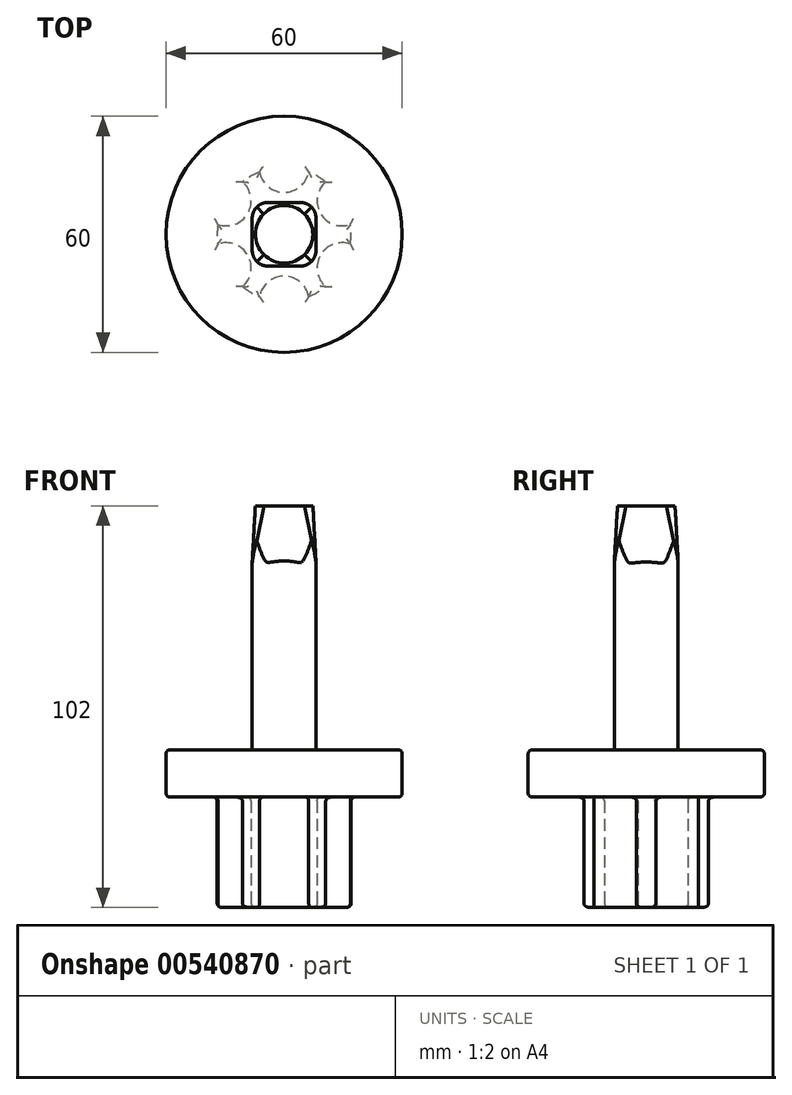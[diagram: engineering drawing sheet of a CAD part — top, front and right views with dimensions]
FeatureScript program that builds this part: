
annotation { "Feature Type Name" : "Feature", "Feature Type Description" : "" }
export const myFeature = defineFeature(function(context is Context, id is Id, definition is map)
    precondition{}
    {
        {
            var Q0;
            Q0=qCreatedBy(makeId("Top.planeOp"),FACE);
            var sketch = newSketch(context, id + "F0", { "sketchPlane" : qUnion([Q0])});
            skCircle(sketch, "E0", {"center": v(0, 0) * mm, "radius": 17 * mm});
            skCircle(sketch, "E1", {"center": v(0, 0) * mm, "radius": 30 * mm});
            skLineSegment(sketch, "E2.bottom", {"start": v(8.1, -8.1) * mm, "end": v(-8.1, -8.1) * mm});
            skLineSegment(sketch, "E2.top", {"start": v(8.1, 8.1) * mm, "end": v(-8.1, 8.1) * mm});
            skLineSegment(sketch, "E2.left", {"start": v(8.1, -8.1) * mm, "end": v(8.1, 8.1) * mm});
            skLineSegment(sketch, "E2.right", {"start": v(-8.1, -8.1) * mm, "end": v(-8.1, 8.1) * mm});
            skCircle(sketch, "E3", {"center": v(0, 0) * mm, "radius": 7 * mm});
            skSolve(sketch);
        }
        {
            var Q0;
            Q0=qCreatedBy(makeId("Top.planeOp"),FACE);
            cPlane(context, id + "F1", {"entities" : qUnion([Q0]), "cplaneType" : CPlaneType.OFFSET, "offset" : 47 * mm, "width" : 150 * mm, "height" : 150 * mm});
        }
        {
            var Q0;
            Q0=qCreatedBy(id+"F1.planeOp",FACE);
            cPlane(context, id + "F2", {"entities" : qUnion([Q0]), "cplaneType" : CPlaneType.OFFSET, "offset" : 15 * mm, "width" : 150 * mm, "height" : 150 * mm});
        }
        {
            var Q0;
            Q0=makeQuery(id+"F0.imprint","IMPRINT",FACE,{"disambiguationData":[TD([[makeQuery(id+"F0.imprint","IMPRINT",EDGE,{"derivedFrom":sQuery(id+"F0.wireOp",EDGE,"E2.bottom")}),-1.0]])]});
            var Q1;
            Q1=makeQuery(id+"F0.imprint","IMPRINT",FACE,{"disambiguationData":[TD([[makeQuery(id+"F0.imprint","IMPRINT",EDGE,{"derivedFrom":sQuery(id+"F0.wireOp",EDGE,"E3")}),1.0]])]});
            var Q2;
            Q2=qCreatedBy(id+"F2.planeOp",FACE);
            extrude(context, id + "F3", {"entities" : qUnion([Q0, Q1]), "endBound" : BoundingType.UP_TO_SURFACE, "depth" : 60 * mm, "endBoundEntityFace" : qUnion([Q2]), "offsetDistance" : 25 * mm});
        }
        {
            var Q0;
            Q0=makeQuery(id+"F3.opExtrude","SWEPT_EDGE",EDGE,{"disambiguationData":[OSD([sQuery(id+"F0.wireOp",EDGE,"E2.bottom"),sQuery(id+"F0.wireOp",EDGE,"E2.left")])]});
            var Q1;
            Q1=makeQuery(id+"F3.opExtrude","SWEPT_EDGE",EDGE,{"disambiguationData":[OSD([sQuery(id+"F0.wireOp",EDGE,"E2.top"),sQuery(id+"F0.wireOp",EDGE,"E2.left")])]});
            var Q2;
            Q2=makeQuery(id+"F3.opExtrude","SWEPT_EDGE",EDGE,{"disambiguationData":[OSD([sQuery(id+"F0.wireOp",EDGE,"E2.bottom"),sQuery(id+"F0.wireOp",EDGE,"E2.right")])]});
            var Q3;
            Q3=makeQuery(id+"F3.opExtrude","SWEPT_EDGE",EDGE,{"disambiguationData":[OSD([sQuery(id+"F0.wireOp",EDGE,"E2.top"),sQuery(id+"F0.wireOp",EDGE,"E2.right")])]});
            fillet(context, id + "F4", {"entities" : qUnion([Q0, Q1, Q2, Q3]), "radius" : 4 * mm, "tangentPropagation" : true, "allowEdgeOverflow" : false});
        }
        {
            var Q0;
            Q0=makeQuery(id+"F0.imprint","IMPRINT",FACE,{"disambiguationData":[TD([[makeQuery(id+"F0.imprint","IMPRINT",EDGE,{"derivedFrom":sQuery(id+"F0.wireOp",EDGE,"E0")}),1.0]])]});
            var sketch = newSketch(context, id + "F5", { "sketchPlane" : qUnion([Q0])});
            skSolve(sketch);
        }
        {
            var Q0;
            Q0=makeQuery(id+"F0.imprint","IMPRINT",FACE,{"disambiguationData":[TD([[makeQuery(id+"F0.imprint","IMPRINT",EDGE,{"derivedFrom":sQuery(id+"F0.wireOp",EDGE,"E0")}),1.0]])]});
            extrude(context, id + "F6", {"entities" : qUnion([Q0]), "oppositeDirection" : true, "depth" : 57.7 * mm, "offsetDistance" : 25 * mm});
        }
        {
            var Q0;
            Q0=makeQuery(id+"F0.imprint","IMPRINT",FACE,{"disambiguationData":[TD([[makeQuery(id+"F0.imprint","IMPRINT",EDGE,{"derivedFrom":sQuery(id+"F0.wireOp",EDGE,"E0")}),-1.0]])]});
            var Q1;
            Q1=makeQuery(id+"F5.imprint","IMPRINT",FACE,{"disambiguationData":[TD([[makeQuery(id+"F5.imprint","IMPRINT",EDGE,{"derivedFrom":makeQuery(id+"F0.imprint","IMPRINT",EDGE,{"derivedFrom":sQuery(id+"F0.wireOp",EDGE,"E2.bottom")})}),-1.0]])]});
            extrude(context, id + "F7", {"entities" : qUnion([Q0, Q1]), "operationType" : NewBodyOperationType.ADD, "oppositeDirection" : true, "depth" : 15 * mm, "offsetDistance" : 25 * mm});
        }
        {
            var Q0;
            Q0=qCreatedBy(id+"F2.planeOp",FACE);
            var sketch = newSketch(context, id + "F8", { "sketchPlane" : qUnion([Q0])});
            skCircle(sketch, "E4", {"center": v(0, 0) * mm, "radius": 7.3 * mm});
            skSolve(sketch);
        }
        {
            var Q0;
            Q0=qCreatedBy(id+"F1.planeOp",FACE);
            var sketch = newSketch(context, id + "F9", { "sketchPlane" : qUnion([Q0])});
            skLineSegment(sketch, "E5.bottom", {"start": v(-8.14, -8.16) * mm, "end": v(8.14, -8.16) * mm});
            skLineSegment(sketch, "E5.top", {"start": v(-8.14, 8.16) * mm, "end": v(8.14, 8.16) * mm});
            skLineSegment(sketch, "E5.left", {"start": v(-8.14, -8.16) * mm, "end": v(-8.14, 8.16) * mm});
            skLineSegment(sketch, "E5.right", {"start": v(8.14, -8.16) * mm, "end": v(8.14, 8.16) * mm});
            skPoint(sketch, "E5.middle", {"position": v(0, 0) * mm});
            skSolve(sketch);
        }
        {
            var Q1;
            Q1=makeQuery(id+"F8.imprint","IMPRINT",FACE,{"disambiguationData":[TD([[makeQuery(id+"F8.imprint","IMPRINT",EDGE,{"derivedFrom":sQuery(id+"F8.wireOp",EDGE,"E4")}),1.0]])]});
            var Q2;
            Q2 = qSketchRegion(id + "F9", true);
            loft(context, id + "F10", {"operationType" : NewBodyOperationType.INTERSECT, "sheetProfilesArray" : [{ "sheetProfileEntities" : qUnion([Q1]) }, { "sheetProfileEntities" : qUnion([Q2]) }]});
        }
        {
            var Q0;
            Q0=makeQuery(id+"F0.imprint","IMPRINT",FACE,{"disambiguationData":[TD([[makeQuery(id+"F0.imprint","IMPRINT",EDGE,{"derivedFrom":sQuery(id+"F0.wireOp",EDGE,"E2.bottom")}),-1.0]])]});
            var Q1;
            Q1=makeQuery(id+"F0.imprint","IMPRINT",FACE,{"disambiguationData":[TD([[makeQuery(id+"F0.imprint","IMPRINT",EDGE,{"derivedFrom":sQuery(id+"F0.wireOp",EDGE,"E3")}),1.0]])]});
            var Q2;
            Q2=qCreatedBy(id+"F1.planeOp",FACE);
            extrude(context, id + "F11", {"entities" : qUnion([Q0, Q1]), "operationType" : NewBodyOperationType.ADD, "endBound" : BoundingType.UP_TO_SURFACE, "depth" : 25 * mm, "endBoundEntityFace" : qUnion([Q2]), "offsetDistance" : 25 * mm});
        }
        {
            var Q0;
            Q0=makeQuery(id+"F11.opExtrude","SWEPT_EDGE",EDGE,{"disambiguationData":[OSD([sQuery(id+"F0.wireOp",EDGE,"E2.top"),sQuery(id+"F0.wireOp",EDGE,"E2.right")])]});
            var Q1;
            Q1=makeQuery(id+"F11.opExtrude","SWEPT_EDGE",EDGE,{"disambiguationData":[OSD([sQuery(id+"F0.wireOp",EDGE,"E2.top"),sQuery(id+"F0.wireOp",EDGE,"E2.left")])]});
            var Q2;
            Q2=makeQuery(id+"F11.opExtrude","SWEPT_EDGE",EDGE,{"disambiguationData":[OSD([sQuery(id+"F0.wireOp",EDGE,"E2.bottom"),sQuery(id+"F0.wireOp",EDGE,"E2.right")])]});
            var Q3;
            Q3=makeQuery(id+"F11.opExtrude","SWEPT_EDGE",EDGE,{"disambiguationData":[OSD([sQuery(id+"F0.wireOp",EDGE,"E2.bottom"),sQuery(id+"F0.wireOp",EDGE,"E2.left")])]});
            fillet(context, id + "F12", {"entities" : qUnion([Q0, Q1, Q2, Q3]), "radius" : 4 * mm, "tangentPropagation" : true, "allowEdgeOverflow" : false});
        }
        {
            var Q0;
            Q0=makeQuery(id+"F0.imprint","IMPRINT",FACE,{"disambiguationData":[TD([[makeQuery(id+"F0.imprint","IMPRINT",EDGE,{"derivedFrom":sQuery(id+"F0.wireOp",EDGE,"E0")}),1.0]])]});
            var Q1;
            Q1=makeQuery(id+"F0.imprint","IMPRINT",FACE,{"disambiguationData":[TD([[makeQuery(id+"F0.imprint","IMPRINT",EDGE,{"derivedFrom":sQuery(id+"F0.wireOp",EDGE,"E3")}),1.0]])]});
            var Q2;
            Q2=makeQuery(id+"F0.imprint","IMPRINT",FACE,{"disambiguationData":[TD([[makeQuery(id+"F0.imprint","IMPRINT",EDGE,{"derivedFrom":sQuery(id+"F0.wireOp",EDGE,"E2.bottom")}),-1.0]])]});
            extrude(context, id + "F13", {"entities" : qUnion([Q0, Q1, Q2]), "operationType" : NewBodyOperationType.ADD, "oppositeDirection" : true, "depth" : 40 * mm, "offsetDistance" : 25 * mm});
        }
        {
            var Q0;
            Q0=makeQuery(id+"F0.imprint","IMPRINT",FACE,{"disambiguationData":[TD([[makeQuery(id+"F0.imprint","IMPRINT",EDGE,{"derivedFrom":sQuery(id+"F0.wireOp",EDGE,"E0")}),-1.0]])]});
            extrude(context, id + "F14", {"entities" : qUnion([Q0]), "operationType" : NewBodyOperationType.ADD, "oppositeDirection" : true, "depth" : 12 * mm, "offsetDistance" : 25 * mm});
        }
        {
            var Q0;
            Q0=makeQuery(id+"F13.opExtrude","CAP_FACE",FACE,{"disambiguationData":[OSD([sQuery(id+"F0.wireOp",EDGE,"E0")])],"isStart":false});
            var sketch = newSketch(context, id + "F15", { "sketchPlane" : qUnion([Q0])});
            skCircle(sketch, "E6", {"center": v(0, 17) * mm, "radius": 6.35 * mm});
            skCircle(sketch, "E7.1.0", {"center": v(-14.72, 8.5) * mm, "radius": 6.35 * mm});
            skCircle(sketch, "E7.2.0", {"center": v(-14.72, -8.5) * mm, "radius": 6.35 * mm});
            skCircle(sketch, "E7.3.0", {"center": v(0, -17) * mm, "radius": 6.35 * mm});
            skCircle(sketch, "E7.4.0", {"center": v(14.72, -8.5) * mm, "radius": 6.35 * mm});
            skCircle(sketch, "E7.5.0", {"center": v(14.72, 8.5) * mm, "radius": 6.35 * mm});
            skPoint(sketch, "E7.center", {"position": v(0, 0) * mm});
            skSolve(sketch);
        }
        {
            var Q0;
            Q0 = qSketchRegion(id + "F15", true);
            var Q1;
            Q1=makeQuery(id+"F14.opExtrude","CAP_FACE",FACE,{"disambiguationData":[OSD([sQuery(id+"F0.wireOp",EDGE,"E0"),sQuery(id+"F0.wireOp",EDGE,"E1")])],"isStart":false});
            extrude(context, id + "F16", {"entities" : qUnion([Q0]), "operationType" : NewBodyOperationType.REMOVE, "endBound" : BoundingType.UP_TO_SURFACE, "oppositeDirection" : true, "depth" : 25 * mm, "endBoundEntityFace" : qUnion([Q1]), "offsetDistance" : 25 * mm});
        }
        {
            var Q0;
            Q0=makeQuery(id+"F13.opExtrude","CAP_FACE",FACE,{"disambiguationData":[OSD([sQuery(id+"F0.wireOp",EDGE,"E0")])],"isStart":false});
            var Q1;
            {var subQ0=sQuery(id+"F0.wireOp",EDGE,"E1");var subQ1=sQuery(id+"F0.wireOp",EDGE,"E0");Q1=makeQuery(id+"F16.boolean.opBoolean","MERGE",FACE,{"derivedFrom":[makeQuery(id+"F14.opExtrude","CAP_FACE",FACE,{"disambiguationData":[OSD([subQ1,subQ0])],"isStart":false}),makeQuery(id+"F16.opExtrude","CAP_FACE",FACE,{"disambiguationData":[OSD([subQ1,subQ0]),OD(0.0)],"isStart":false}),makeQuery(id+"F16.opExtrude","CAP_FACE",FACE,{"disambiguationData":[OSD([subQ1,subQ0]),OD(1.0)],"isStart":false}),makeQuery(id+"F16.opExtrude","CAP_FACE",FACE,{"disambiguationData":[OSD([subQ1,subQ0]),OD(2.0)],"isStart":false}),makeQuery(id+"F16.opExtrude","CAP_FACE",FACE,{"disambiguationData":[OSD([subQ1,subQ0]),OD(3.0)],"isStart":false}),makeQuery(id+"F16.opExtrude","CAP_FACE",FACE,{"disambiguationData":[OSD([subQ1,subQ0]),OD(4.0)],"isStart":false}),makeQuery(id+"F16.opExtrude","CAP_FACE",FACE,{"disambiguationData":[OSD([subQ1,subQ0]),OD(5.0)],"isStart":false})]});}
            var Q2;
            Q2=makeQuery(id+"F14.opExtrude","CAP_EDGE",EDGE,{"disambiguationData":[OSD([sQuery(id+"F0.wireOp",EDGE,"E1")])],"isStart":false});
            var Q3;
            Q3=makeQuery(id+"F14.opExtrude","CAP_EDGE",EDGE,{"disambiguationData":[OSD([sQuery(id+"F0.wireOp",EDGE,"E1")])],"isStart":true});
            var Q4;
            Q4=makeQuery(id+"F3.opExtrude","CAP_FACE",FACE,{"disambiguationData":[OSD([dummyQuery(id+"F2.planeOp",FACE)])],"isStart":false});
            fillet(context, id + "F17", {"entities" : qUnion([Q0, Q1, Q2, Q3, Q4]), "radius" : 1 * mm, "tangentPropagation" : true, "allowEdgeOverflow" : false});
        }
    });
